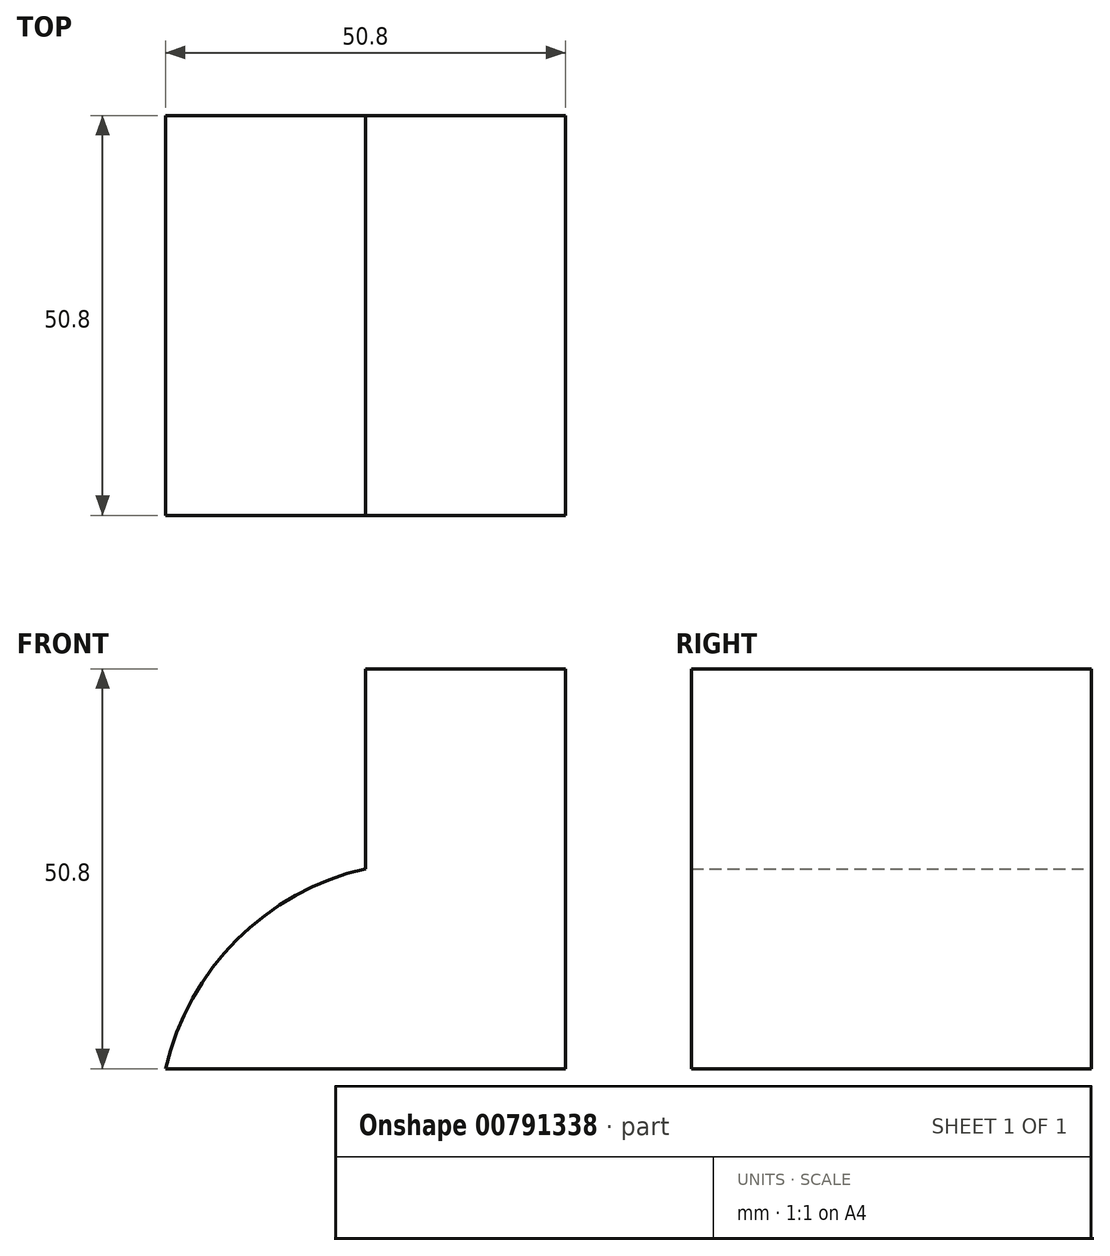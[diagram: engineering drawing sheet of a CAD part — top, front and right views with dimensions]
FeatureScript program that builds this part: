
annotation { "Feature Type Name" : "Feature", "Feature Type Description" : "" }
export const myFeature = defineFeature(function(context is Context, id is Id, definition is map)
    precondition{}
    {
        {
            var Q0;
            Q0=qCreatedBy(makeId("Front.planeOp"),FACE);
            var sketch = newSketch(context, id + "F0", { "sketchPlane" : qUnion([Q0])});
            skLineSegment(sketch, "E0", {"start": v(0, 0) * mm, "end": v(50.8, 0) * mm});
            skLineSegment(sketch, "E1", {"start": v(50.8, 0) * mm, "end": v(50.8, 50.8) * mm});
            skLineSegment(sketch, "E2", {"start": v(50.8, 50.8) * mm, "end": v(25.4, 50.8) * mm});
            skLineSegment(sketch, "E3", {"start": v(25.4, 50.8) * mm, "end": v(25.4, 25.4) * mm});
            skArc(sketch, "E4", {"start": v(25.4, 25.4) * mm, "mid": v(9.04, 16.36) * mm, "end": v(0, 0) * mm});
            skSolve(sketch);
        }
        {
            var Q0;
            Q0=qSketchRegion(id+"F0",true);
            extrude(context, id + "F1", {"entities" : qUnion([Q0]), "depth" : 50.8 * mm, "offsetDistance" : 25.4 * mm});
        }
    });
